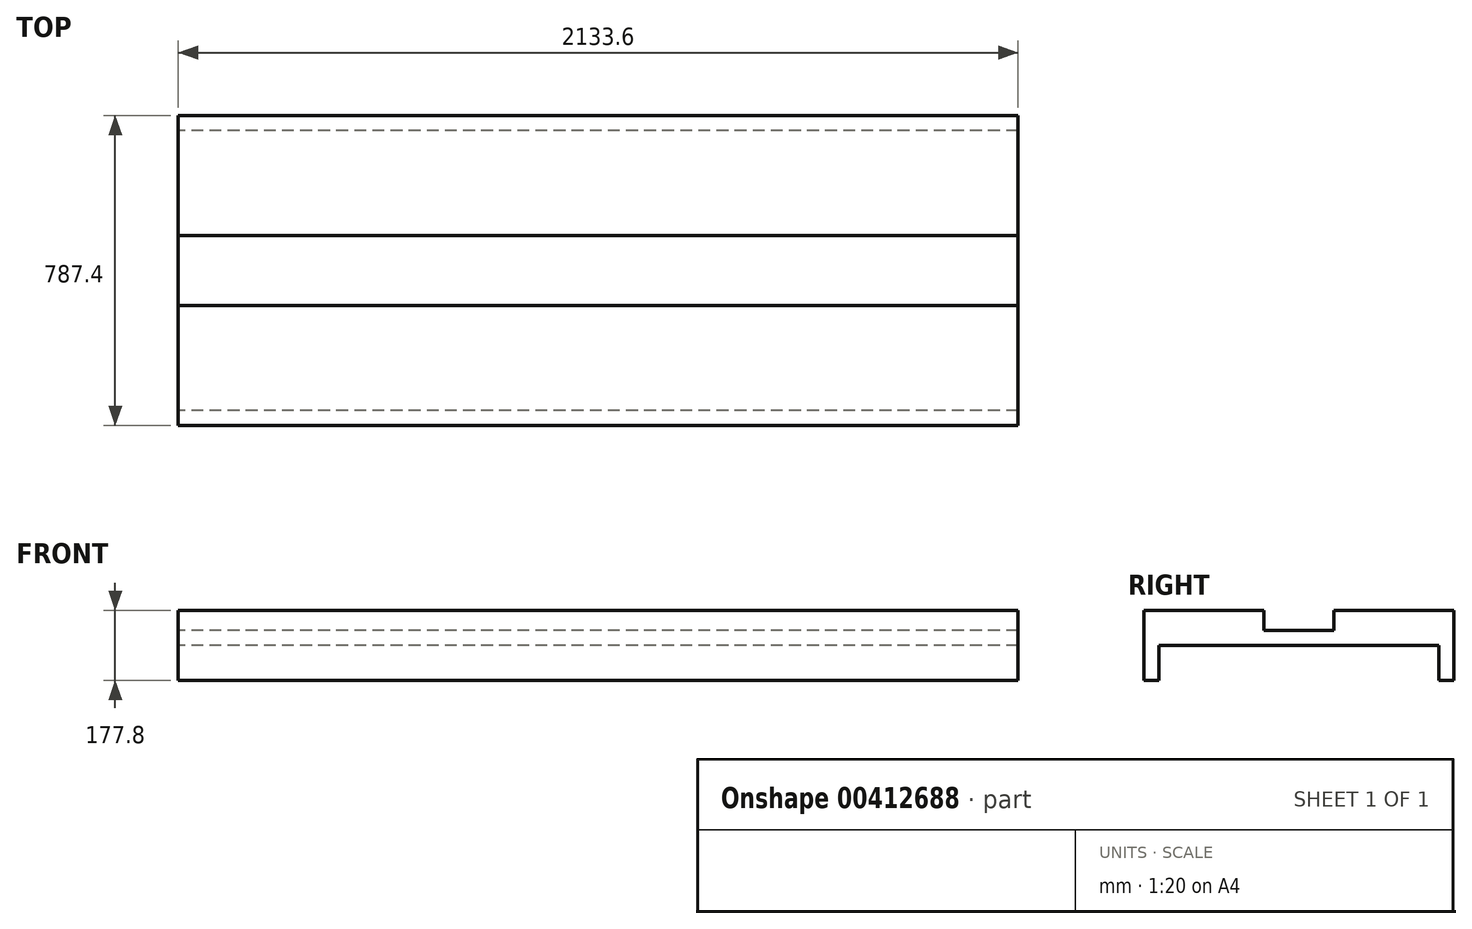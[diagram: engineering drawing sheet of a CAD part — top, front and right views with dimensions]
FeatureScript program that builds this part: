
annotation { "Feature Type Name" : "Feature", "Feature Type Description" : "" }
export const myFeature = defineFeature(function(context is Context, id is Id, definition is map)
    precondition{}
    {
        {
            var Q0;
            Q0=qCreatedBy(makeId("Right.planeOp"),FACE);
            var sketch = newSketch(context, id + "F0", { "sketchPlane" : qUnion([Q0])});
            skLineSegment(sketch, "E0.bottom", {"start": v(0, 0) * mm, "end": v(266.7, 0) * mm});
            skLineSegment(sketch, "E0.top", {"start": v(0, 88.9) * mm, "end": v(266.7, 88.9) * mm});
            skLineSegment(sketch, "E0.left", {"start": v(0, 0) * mm, "end": v(0, 88.9) * mm});
            skLineSegment(sketch, "E0.right", {"start": v(266.7, 0) * mm, "end": v(266.7, 88.9) * mm});
            skLineSegment(sketch, "E1.bottom", {"start": v(0, 0) * mm, "end": v(-177.8, 0) * mm});
            skLineSegment(sketch, "E1.top", {"start": v(0, 38.1) * mm, "end": v(-177.8, 38.1) * mm});
            skLineSegment(sketch, "E1.left", {"start": v(0, 0) * mm, "end": v(0, 38.1) * mm});
            skLineSegment(sketch, "E1.right", {"start": v(-177.8, 0) * mm, "end": v(-177.8, 38.1) * mm});
            skLineSegment(sketch, "E2.bottom", {"start": v(-177.8, 0) * mm, "end": v(-444.5, 0) * mm});
            skLineSegment(sketch, "E2.top", {"start": v(-177.8, 88.9) * mm, "end": v(-444.5, 88.9) * mm});
            skLineSegment(sketch, "E2.left", {"start": v(-177.8, 0) * mm, "end": v(-177.8, 88.9) * mm});
            skLineSegment(sketch, "E2.right", {"start": v(-444.5, 0) * mm, "end": v(-444.5, 88.9) * mm});
            skLineSegment(sketch, "E3.bottom", {"start": v(266.7, 88.9) * mm, "end": v(304.8, 88.9) * mm});
            skLineSegment(sketch, "E3.top", {"start": v(266.7, -88.9) * mm, "end": v(304.8, -88.9) * mm});
            skLineSegment(sketch, "E3.left", {"start": v(266.7, 88.9) * mm, "end": v(266.7, -88.9) * mm});
            skLineSegment(sketch, "E3.right", {"start": v(304.8, 88.9) * mm, "end": v(304.8, -88.9) * mm});
            skLineSegment(sketch, "E4.bottom", {"start": v(-444.5, 88.9) * mm, "end": v(-482.6, 88.9) * mm});
            skLineSegment(sketch, "E4.top", {"start": v(-444.5, -88.9) * mm, "end": v(-482.6, -88.9) * mm});
            skLineSegment(sketch, "E4.left", {"start": v(-444.5, 88.9) * mm, "end": v(-444.5, -88.9) * mm});
            skLineSegment(sketch, "E4.right", {"start": v(-482.6, 88.9) * mm, "end": v(-482.6, -88.9) * mm});
            skSolve(sketch);
        }
        {
            var Q0;
            Q0 = qSketchRegion(id + "F0", true);
            extrude(context, id + "F1", {"entities" : qUnion([Q0]), "depth" : 2133.6 * mm});
        }
    });
